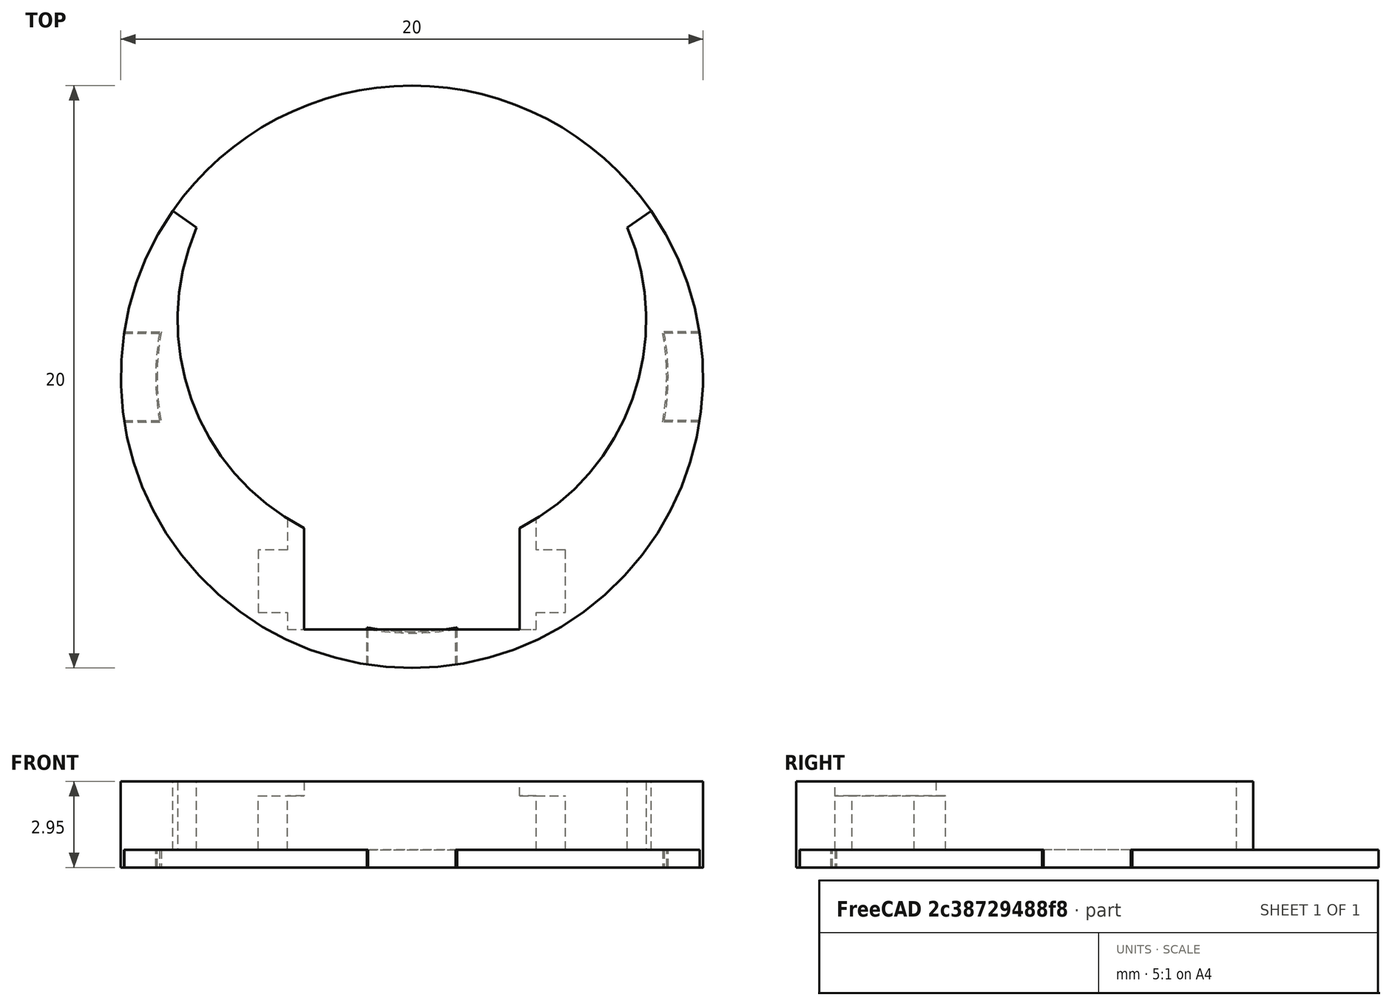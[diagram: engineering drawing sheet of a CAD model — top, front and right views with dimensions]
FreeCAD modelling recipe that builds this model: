
FCSTD DOCUMENT  (FreeCAD 0.18R)
Label: model
License: All rights reserved
LicenseURL: http://en.wikipedia.org/wiki/All_rights_reserved
objects: PartDesign::Body×6, Sketcher::SketchObject×5, PartDesign::Pad×5, App::Part×2, PartDesign::FeatureBase×2, Part::MultiFuse×2, Mesh::Feature×2, Spreadsheet::Sheet×1, Part::Cut×1
note: 26 computed .brp shape members not serialized (recipe doc carries the construction recipe); baked Part::Feature solids carry a one-line shape summary decoded from their .brp

FEATURE [Sketcher::SketchObject] Sketch
  MapMode = 5
  Support = -> [XY_Plane001]
  expr: Constraints[19] = data.alignment_pin_length / 2 + data.interference_gap
  expr: Constraints[18] = data.alignment_pin_length / 2 + data.interference_gap
  expr: Constraints[17] = data.alignment_pin_length / 2 + data.interference_gap
  expr: Constraints[16] = data.alignment_pin_length / 2 + data.interference_gap
  expr: Constraints[11] = data.outer_battery_radius - Spreadsheet.alignment_pin_width - data.interference_gap
  expr: Constraints[1] = data.outer_battery_radius
  sketch-geometry (18):
    g0: Circle [constr] CenterX=0 CenterY=0 CenterZ=0 NormalX=0 NormalY=0 NormalZ=1 AngleXU=0 Radius=10
    g1: LineSegment [constr] StartX=1.55 StartY=9.87914 StartZ=0 EndX=1.55 EndY=-9.87914 EndZ=0
    g2: LineSegment [constr] StartX=9.87914 StartY=1.55 StartZ=0 EndX=-9.87914 EndY=1.55 EndZ=0
    g3: LineSegment [constr] StartX=9.87914 StartY=-1.55 StartZ=0 EndX=-9.87914 EndY=-1.55 EndZ=0
    g4: LineSegment [constr] StartX=-1.55 StartY=9.87914 StartZ=0 EndX=-1.55 EndY=-9.87914 EndZ=0
    g5: Circle [constr] CenterX=0 CenterY=0 CenterZ=0 NormalX=0 NormalY=0 NormalZ=1 AngleXU=0 Radius=8.75
    g6: ArcOfCircle CenterX=0 CenterY=0 CenterZ=0 NormalX=0 NormalY=0 NormalZ=1 AngleXU=0 Radius=10 StartAngle=0.155627 EndAngle=2.98597
    g7: ArcOfCircle CenterX=0 CenterY=0 CenterZ=0 NormalX=0 NormalY=0 NormalZ=1 AngleXU=0 Radius=10 StartAngle=3.29722 EndAngle=4.55676
    g8: ArcOfCircle CenterX=0 CenterY=0 CenterZ=0 NormalX=0 NormalY=0 NormalZ=1 AngleXU=0 Radius=10 StartAngle=4.86802 EndAngle=6.12756
    g9: ArcOfCircle CenterX=0 CenterY=0 CenterZ=0 NormalX=0 NormalY=0 NormalZ=1 AngleXU=0 Radius=8.75 StartAngle=2.96351 EndAngle=3.31968
    g10: ArcOfCircle CenterX=0 CenterY=0 CenterZ=0 NormalX=0 NormalY=0 NormalZ=1 AngleXU=0 Radius=8.75 StartAngle=6.1051 EndAngle=6.46127
    g11: ArcOfCircle CenterX=0 CenterY=0 CenterZ=0 NormalX=0 NormalY=0 NormalZ=1 AngleXU=0 Radius=8.75 StartAngle=4.53431 EndAngle=4.89047
    g12: LineSegment StartX=-9.87914 StartY=1.55 StartZ=0 EndX=-8.61162 EndY=1.55 EndZ=0
    g13: LineSegment StartX=-9.87914 StartY=-1.55 StartZ=0 EndX=-8.61162 EndY=-1.55 EndZ=0
    g14: LineSegment StartX=-1.55 StartY=-9.87914 StartZ=0 EndX=-1.55 EndY=-8.61162 EndZ=0
    g15: LineSegment StartX=1.55 StartY=-9.87914 StartZ=0 EndX=1.55 EndY=-8.61162 EndZ=0
    g16: LineSegment StartX=9.87914 StartY=-1.55 StartZ=0 EndX=8.61162 EndY=-1.55 EndZ=0
    g17: LineSegment StartX=9.87914 StartY=1.55 StartZ=0 EndX=8.61162 EndY=1.55 EndZ=0
  constraints (53):
    c: Coincident(g0,g-1)
    c: Radius(g0) = 10
    c: PointOnObject(g1,g0)
    c: PointOnObject(g1,g0)
    c: PointOnObject(g2,g0)
    c: PointOnObject(g2,g0)
    c: PointOnObject(g3,g0)
    c: PointOnObject(g3,g0)
    c: PointOnObject(g4,g0)
    c: PointOnObject(g4,g0)
    c: Coincident(g5,g-1)
    c: Radius(g5) = 8.75
    c: Horizontal(g3)
    c: Horizontal(g2)
    c: Vertical(g4)
    c: Vertical(g1)
    c: DistanceY(g-1,g2) = 1.55
    c: DistanceY(g3,g-1) = 1.55
    c: DistanceX(g4,g-1) = 1.55
    c: DistanceX(g-1,g1) = 1.55
    c: Coincident(g6,g-1)
    c: Coincident(g6,g2)
    c: PointOnObject(g6,g2)
    c: Coincident(g7,g6)
    c: Coincident(g7,g4)
    c: PointOnObject(g7,g3)
    c: Coincident(g8,g6)
    c: Coincident(g8,g3)
    c: PointOnObject(g8,g1)
    c: Coincident(g9,g6)
    c: PointOnObject(g9,g3)
    c: PointOnObject(g9,g2)
    c: Coincident(g10,g6)
    c: PointOnObject(g10,g2)
    c: PointOnObject(g10,g3)
    c: Coincident(g11,g6)
    c: PointOnObject(g11,g1)
    c: PointOnObject(g11,g4)
    c: PointOnObject(g9,g5)
    c: PointOnObject(g10,g5)
    c: PointOnObject(g11,g5)
    c: Coincident(g12,g6)
    c: Coincident(g12,g9)
    c: Coincident(g13,g7)
    c: Coincident(g13,g9)
    c: Coincident(g14,g7)
    c: Coincident(g14,g11)
    c: Coincident(g15,g8)
    c: Coincident(g15,g11)
    c: Coincident(g16,g8)
    c: Coincident(g16,g10)
    c: Coincident(g17,g6)
    c: Coincident(g17,g10)
FEATURE [Spreadsheet::Sheet] Spreadsheet  label="data"
  cells = A1=outer_battery_radius; B1(outer_battery_radius)==20mm / 2; A2=inner_battery_radius; B2(inner_battery_radius)==16mm / 2; A3=board_thickness; B3(board_thickness)==0.59999999999999998mm; A4=alignment_pin_width; B4(alignment_pin_width)==1.2000000000000002mm; A5=alignment_pin_length; B5(alignment_pin_length)==3mm; A6=interference_gap; B6(interference_gap)==0.050000000000000003mm; A7=case_end_width; B7(case_end_width)==1mm; A8=outer_battery_thickness; B8(outer_battery_thickness)==3.2000000000000002mm; A9=inner_battery_thickness; B9(inner_battery_thickness)==2mm; A10=reed_switch_base_length; B10(reed_switch_base_length)==reed_switch_length - 1mm * 2; A11=soldering_error; B11(soldering_error)==0.5mm; A12=reed_switch_width; B12(reed_switch_width)==2.3100000000000001mm; A13=reed_switch_base_height; B13(reed_switch_base_height)==2.3100000000000001mm / 2 + 0.20000000000000001mm; A14=reed_switch_height; B14(reed_switch_height)==2.3100000000000001mm + 0.080000000000000002mm; A15=reed_switch_body_length; B15(reed_switch_body_length)==6.4000000000000004mm; A16=case_wall_thickness; B16(case_wall_thickness)==0.5mm; A17=reed_switch_lead_width; B17(reed_switch_lead_width)==1.1399999999999999mm; A18=reed_switch_length; B18(reed_switch_length)==9.5500000000000007mm; A19="case_coupling_overhead"; B19(case_coupling_overhead)==0.25mm
FEATURE [PartDesign::Pad] Pad
  Length = 0.6
  Length2 = 100
  Profile = -> Sketch
  Reversed = true
  Type = 0
  expr: Length = data.board_thickness
FEATURE [PartDesign::Body] Body  label="board_body"
  Group = -> [Sketch,Pad]
  Origin = -> Origin001
  Tip = -> Pad
FEATURE [App::Part] Part  label="board_part"
  Group = -> [Body]
  Origin = -> Origin
FEATURE [Sketcher::SketchObject] Sketch001
  MapMode = 5
  Support = -> [XY_Plane003]
  expr: Constraints[16] = data.case_end_width
  expr: Constraints[15] = data.case_end_width
  expr: Constraints[10] = data.inner_battery_radius + data.interference_gap
  expr: Constraints[1] = data.outer_battery_radius
  sketch-geometry (11):
    g0: Circle [constr] CenterX=0 CenterY=0 CenterZ=0 NormalX=0 NormalY=0 NormalZ=1 AngleXU=0 Radius=10
    g1: LineSegment [constr] StartX=0 StartY=0 StartZ=0 EndX=-8.21783 EndY=5.69801 EndZ=0
    g2: LineSegment [constr] StartX=0 StartY=0 StartZ=0 EndX=8.21783 EndY=5.69801 EndZ=0
    g3: Circle [constr] CenterX=0 CenterY=1.95 CenterZ=0 NormalX=0 NormalY=0 NormalZ=1 AngleXU=0 Radius=8.05
    g4: GeomPoint X=0 Y=10 Z=0
    g5: GeomPoint X=-7.39605 Y=5.12821 Z=0
    g6: GeomPoint X=7.39605 Y=5.12821 Z=0
    g7: ArcOfCircle CenterX=4e-16 CenterY=-1.1e-15 CenterZ=0 NormalX=0 NormalY=0 NormalZ=1 AngleXU=0 Radius=10 StartAngle=2.53533 EndAngle=6.88945
    g8: ArcOfCircle CenterX=2e-16 CenterY=1.95 CenterZ=0 NormalX=0 NormalY=0 NormalZ=1 AngleXU=0 Radius=8.05 StartAngle=2.73573 EndAngle=6.68904
    g9: LineSegment StartX=-8.21783 StartY=5.69801 StartZ=0 EndX=-7.39605 EndY=5.12821 EndZ=0
    g10: LineSegment StartX=7.39605 StartY=5.12821 StartZ=0 EndX=8.21783 EndY=5.69801 EndZ=0
  constraints (27):
    c: Coincident(g0,g-1)
    c: Radius(g0) = 10
    c: Coincident(g1,g-1)
    c: PointOnObject(g1,g0)
    c: Coincident(g2,g-1)
    c: PointOnObject(g2,g0)
    c: PointOnObject(g3,g-2)
    c: PointOnObject(g4,g0)
    c: PointOnObject(g4,g-2)
    c: PointOnObject(g4,g3)
    c: Radius(g3) = 8.05
    c: PointOnObject(g5,g1)
    c: PointOnObject(g6,g2)
    c: PointOnObject(g5,g3)
    c: PointOnObject(g6,g3)
    c: Distance(g5,g1) = 1
    c: Distance(g6,g2) = 1
    c: Coincident(g7,g1)
    c: Coincident(g7,g2)
    c: Tangent(g7,g0)
    c: Coincident(g8,g5)
    c: Coincident(g8,g6)
    c: Tangent(g8,g3)
    c: Coincident(g9,g7)
    c: Coincident(g9,g5)
    c: Coincident(g10,g6)
    c: Coincident(g10,g7)
FEATURE [PartDesign::Pad] Pad001
  Length = 2.35
  Length2 = 100
  Profile = -> Sketch001
  Type = 0
  expr: Length = data.outer_battery_thickness - data.board_thickness - data.case_coupling_overhead
FEATURE [PartDesign::Body] Body001  label="case_whole_body"
  Group = -> [Sketch001,Pad001]
  Origin = -> Origin003
  Tip = -> Pad001
FEATURE [Sketcher::SketchObject] Sketch002
  MapMode = 5
  Support = -> [XY_Plane004]
  expr: Constraints[11] = data.alignment_pin_length / 2
  expr: Constraints[7] = data.outer_battery_radius - Spreadsheet.alignment_pin_width
  expr: Constraints[10] = data.alignment_pin_length / 2
  expr: Constraints[1] = data.outer_battery_radius
  sketch-geometry (8):
    g0: Circle [constr] CenterX=0 CenterY=0 CenterZ=0 NormalX=0 NormalY=0 NormalZ=1 AngleXU=0 Radius=10
    g1: LineSegment [constr] StartX=9.88686 StartY=1.5 StartZ=0 EndX=-9.88686 EndY=1.5 EndZ=0
    g2: LineSegment [constr] StartX=9.88686 StartY=-1.5 StartZ=0 EndX=-9.88686 EndY=-1.5 EndZ=0
    g3: Circle [constr] CenterX=0 CenterY=0 CenterZ=0 NormalX=0 NormalY=0 NormalZ=1 AngleXU=0 Radius=8.8
    g4: LineSegment StartX=9.88686 StartY=-1.5 StartZ=0 EndX=8.67122 EndY=-1.5 EndZ=0
    g5: LineSegment StartX=9.88686 StartY=1.5 StartZ=0 EndX=8.67122 EndY=1.5 EndZ=0
    g6: ArcOfCircle CenterX=0 CenterY=0 CenterZ=0 NormalX=0 NormalY=0 NormalZ=1 AngleXU=0 Radius=8.8 StartAngle=6.11189 EndAngle=6.45448
    g7: ArcOfCircle CenterX=0 CenterY=0 CenterZ=0 NormalX=0 NormalY=0 NormalZ=1 AngleXU=0 Radius=10 StartAngle=6.13262 EndAngle=6.43375
  constraints (24):
    c: Coincident(g0,g-1)
    c: Radius(g0) = 10
    c: PointOnObject(g1,g0)
    c: PointOnObject(g1,g0)
    c: PointOnObject(g2,g0)
    c: PointOnObject(g2,g0)
    c: Coincident(g3,g-1)
    c: Radius(g3) = 8.8
    c: Horizontal(g2)
    c: Horizontal(g1)
    c: DistanceY(g-1,g1) = 1.5
    c: DistanceY(g2,g-1) = 1.5
    c: PointOnObject(g5,g1)
    c: PointOnObject(g4,g2)
    c: PointOnObject(g4,g3)
    c: Coincident(g4,g2)
    c: Coincident(g1,g5)
    c: PointOnObject(g5,g3)
    c: Coincident(g6,g-1)
    c: Coincident(g6,g5)
    c: PointOnObject(g6,g2)
    c: Coincident(g7,g6)
    c: Coincident(g7,g5)
    c: PointOnObject(g7,g2)
FEATURE [PartDesign::Pad] Pad002
  Length = 0.6
  Length2 = 100
  Profile = -> Sketch002
  Reversed = true
  Type = 0
  expr: Length = data.board_thickness
FEATURE [PartDesign::Body] Body002  label="alignment_pin1"
  Group = -> [Sketch002,Pad002]
  Origin = -> Origin004
  Tip = -> Pad002
FEATURE [PartDesign::FeatureBase] Clone
  BaseFeature = -> Body002
FEATURE [PartDesign::Body] Body003  label="alignment_pin2"
  BaseFeature = -> Body002
  Group = -> [Clone]
  Origin = -> Origin005
  Placement = pos=(0,0,0) rot=(0,0,-1;1.5708rad)
  Tip = -> Clone
FEATURE [PartDesign::FeatureBase] Clone001
  BaseFeature = -> Body002
FEATURE [PartDesign::Body] Body004  label="alignment_pin3"
  BaseFeature = -> Body002
  Group = -> [Clone001]
  Origin = -> Origin006
  Placement = pos=(0,0,0) rot=(0,0,1;3.14159rad)
  Tip = -> Clone001
FEATURE [Part::MultiFuse] Fusion  label="alignment_pins"
  Shapes = -> [Body004,Body003,Body002]
FEATURE [Sketcher::SketchObject] Sketch003
  MapMode = 5
  Support = -> [XY_Plane007]
  expr: Constraints[54] = (data.reed_switch_width - data.reed_switch_lead_width) / 2
  expr: Constraints[48] = (data.reed_switch_width - data.reed_switch_lead_width) / 2
  expr: Constraints[45] = data.reed_switch_base_length + data.soldering_error * 2
  expr: Constraints[43] = data.reed_switch_length + data.soldering_error * 2
  expr: Constraints[40] = data.reed_switch_lead_width + data.soldering_error * 2
  expr: Constraints[1] = data.outer_battery_radius
  expr: Constraints[13] = data.alignment_pin_length
  expr: Constraints[6] = data.outer_battery_radius - data.alignment_pin_width
  expr: Constraints[4] = data.inner_battery_radius + data.interference_gap
  sketch-geometry (20):
    g0: Circle [constr] CenterX=0 CenterY=0 CenterZ=0 NormalX=0 NormalY=0 NormalZ=1 AngleXU=0 Radius=10
    g1: Circle [constr] CenterX=0 CenterY=1.95 CenterZ=0 NormalX=0 NormalY=0 NormalZ=1 AngleXU=0 Radius=8.05
    g2: Circle [constr] CenterX=0 CenterY=0 CenterZ=0 NormalX=0 NormalY=0 NormalZ=1 AngleXU=0 Radius=8.8
    g3: LineSegment [constr] StartX=-1.5 StartY=-9.88686 StartZ=0 EndX=-1.5 EndY=9.88686 EndZ=0
    g4: LineSegment [constr] StartX=1.5 StartY=9.88686 StartZ=0 EndX=1.5 EndY=-9.88686 EndZ=0
    g5: GeomPoint X=-1.5 Y=-8.67122 Z=0
    g6: GeomPoint X=1.5 Y=-8.67122 Z=0
    g7: LineSegment StartX=-4.275 StartY=-8.67122 StartZ=0 EndX=4.275 EndY=-8.67122 EndZ=0
    g8: LineSegment StartX=4.275 StartY=-8.67122 StartZ=0 EndX=4.275 EndY=-8.08622 EndZ=0
    g9: LineSegment StartX=4.275 StartY=-8.08622 StartZ=0 EndX=5.275 EndY=-8.08622 EndZ=0
    g10: LineSegment StartX=5.275 StartY=-8.08622 StartZ=0 EndX=5.275 EndY=-5.94622 EndZ=0
    g11: LineSegment StartX=5.275 StartY=-5.94622 StartZ=0 EndX=4.275 EndY=-5.94622 EndZ=0
    g12: LineSegment StartX=4.275 StartY=-5.94622 StartZ=0 EndX=4.275 EndY=-4.87106 EndZ=0
    g13: LineSegment StartX=4.275 StartY=-4.87106 StartZ=0 EndX=-4.275 EndY=-4.87106 EndZ=0
    g14: LineSegment StartX=-4.275 StartY=-4.87106 StartZ=0 EndX=-4.275 EndY=-5.94622 EndZ=0
    g15: LineSegment StartX=-4.275 StartY=-5.94622 StartZ=0 EndX=-5.275 EndY=-5.94622 EndZ=0
    g16: LineSegment StartX=-5.275 StartY=-5.94622 StartZ=0 EndX=-5.275 EndY=-8.08622 EndZ=0
    g17: LineSegment StartX=-5.275 StartY=-8.08622 StartZ=0 EndX=-4.275 EndY=-8.08622 EndZ=0
    g18: LineSegment StartX=-4.275 StartY=-8.08622 StartZ=0 EndX=-4.275 EndY=-8.67122 EndZ=0
    g19: LineSegment [constr] StartX=-4.275 StartY=-5.36122 StartZ=0 EndX=4.275 EndY=-5.36122 EndZ=0
  constraints (55):
    c: Coincident(g0,g-1)
    c: Radius(g0) = 10
    c: PointOnObject(g1,g-2)
    c: Tangent(g1,g0)
    c: Radius(g1) = 8.05
    c: Coincident(g2,g-1)
    c: Radius(g2) = 8.8
    c: PointOnObject(g3,g0)
    c: PointOnObject(g3,g0)
    c: PointOnObject(g4,g0)
    c: Vertical(g4)
    c: Vertical(g3)
    c: Symmetric(g3,g4,g-2)
    c: Distance(g3,g4) = 3
    c: PointOnObject(g5,g2)
    c: PointOnObject(g5,g3)
    c: PointOnObject(g6,g2)
    c: PointOnObject(g6,g4)
    c: Coincident(g7,g8)
    c: Vertical(g8)
    c: Coincident(g8,g9)
    c: Horizontal(g9)
    c: Coincident(g9,g10)
    c: Vertical(g10)
    c: Coincident(g10,g11)
    c: Horizontal(g11)
    c: Coincident(g11,g12)
    c: Vertical(g12)
    c: Coincident(g12,g13)
    c: Horizontal(g13)
    c: Coincident(g13,g14)
    c: Vertical(g14)
    c: Coincident(g14,g15)
    c: Coincident(g15,g16)
    c: Vertical(g16)
    c: Coincident(g16,g17)
    c: Horizontal(g17)
    c: Coincident(g17,g18)
    c: Coincident(g18,g7)
    c: Vertical(g18)
    c: Distance(g10) = 2.14
    c: Equal(g10,g16)
    c: Symmetric(g16,g9,g-2)
    c: Distance(g9,g16) = 10.55
    c: Symmetric(g7,g7,g-2)
    c: Distance(g7) = 8.55
    c: Equal(g7,g13)
    c: Symmetric(g14,g11,g-2)
    c: Distance(g8) = 0.585
    c: PointOnObject(g5,g7)
    c: PointOnObject(g13,g1)
    c: PointOnObject(g19,g12)
    c: Horizontal(g19)
    c: PointOnObject(g19,g14)
    c: Distance(g14,g19) = 0.585
FEATURE [PartDesign::Pad] Pad003
  Length = 1.855
  Length2 = 100
  Profile = -> Sketch003
  Type = 0
  expr: Length = data.reed_switch_base_height + data.soldering_error
FEATURE [Sketcher::SketchObject] Sketch004
  ExternalGeometry = -> [Pad003]
  MapMode = 5
  Placement = pos=(0,0,1.855) rot=(0,0,1;0rad)
  Support = -> [Pad003]
  expr: Constraints[2] = data.reed_switch_body_length + data.soldering_error * 2
  sketch-geometry (4):
    g0: LineSegment StartX=-3.7 StartY=-8.67122 StartZ=0 EndX=3.7 EndY=-8.67122 EndZ=0
    g1: LineSegment StartX=-3.7 StartY=-8.67122 StartZ=0 EndX=-3.7 EndY=-4.87106 EndZ=0
    g2: LineSegment StartX=-3.7 StartY=-4.87106 StartZ=0 EndX=3.7 EndY=-4.87106 EndZ=0
    g3: LineSegment StartX=3.7 StartY=-4.87106 StartZ=0 EndX=3.7 EndY=-8.67122 EndZ=0
  constraints (11):
    c: PointOnObject(g0,g-3)
    c: Symmetric(g0,g0,g-2)
    c: Distance(g0) = 7.4
    c: Coincident(g0,g1)
    c: Vertical(g1)
    c: Coincident(g1,g2)
    c: Coincident(g2,g3)
    c: Coincident(g3,g0)
    c: Vertical(g3)
    c: Parallel(g2,g0)
    c: PointOnObject(g1,g-4)
FEATURE [PartDesign::Pad] Pad004
  BaseFeature = -> Pad003
  Length = 1.245
  Length2 = 100
  Profile = -> Sketch004
  Type = 0
  expr: Length = data.outer_battery_thickness - data.board_thickness - data.reed_switch_base_height
FEATURE [PartDesign::Body] Body005  label="reed_switch_opening"
  Group = -> [Sketch003,Pad003,Sketch004,Pad004]
  Origin = -> Origin007
  Tip = -> Pad004
FEATURE [Part::Cut] Cut
  Base = -> Body001
  Tool = -> Body005
FEATURE [Part::MultiFuse] Fusion001  label="case_body"
  Shapes = -> [Cut,Fusion]
FEATURE [App::Part] Part001  label="case_part"
  Group = -> [Body001,Body002,Body003,Body004,Fusion,Body005,Cut,Fusion001]
  Origin = -> Origin002
FEATURE [Mesh::Feature] Mesh001  label="board_body (Meshed)"
FEATURE [Mesh::Feature] Mesh  label="case_body (Meshed)"
